FCSTD DOCUMENT  (FreeCAD 0.21R33668 +26 (Git))
Label: RotateEngine-000
License: All rights reserved
LicenseURL: http://en.wikipedia.org/wiki/All_rights_reserved
objects: App::DocumentObjectGroup×3, PartDesign::CoordinateSystem×2, Sketcher::SketchObject×2, App::FeaturePython×1, App::Part×1
note: 4 computed .brp shape members not serialized (recipe doc carries the construction recipe); baked Part::Feature solids carry a one-line shape summary decoded from their .brp

FEATURE [App::DocumentObjectGroup] Parts
FEATURE [PartDesign::CoordinateSystem] LCS_Origin
  AttacherType = Attacher::AttachEngine3D
  MapMode = 3
  Placement = pos=(0,0,0) rot=(1,0,0;3.14159rad)
  Support = -> [XZ_Plane]
FEATURE [App::DocumentObjectGroup] Constraints
FEATURE [App::FeaturePython] Variables  # WARN: FeaturePython — macro-defined, semantics opaque (R4)
  Angle_Rotation = 339
  Type = App::PropertyContainer
FEATURE [App::DocumentObjectGroup] Configurations
FEATURE [Sketcher::SketchObject] Barre  label="Sketch_Engine"
  AttachmentOffset = pos=(0,0,0) rot=(0,0,1;5.91667rad)
  FullyConstrained = false
  MapMode = 3
  Placement = pos=(0,0,0) rot=(0.967324,0.179283,0.179283;4.67917rad)
  Support = -> [LCS_Origin]
  expr: .AttachmentOffset.Rotation.Angle = Variables.Angle_Rotation
  sketch-geometry (2):
    g0: Circle CenterX=0 CenterY=0 CenterZ=0 NormalX=0 NormalY=0 NormalZ=1 AngleXU=0 Radius=20
    g1: LineSegment StartX=0 StartY=0 StartZ=0 EndX=17.8904 EndY=8.94064 EndZ=0
  constraints (4):
    c: Coincident(g0,g-1)
    c: Radius(g0) = 20
    c: Coincident(g1,g0)
    c: PointOnObject(g1,g0)
FEATURE [PartDesign::CoordinateSystem] LCS_Mobile
  AttacherType = Attacher::AttachEngine3D
  AttachmentOffset = pos=(40,0,0) rot=(0,0,1;0rad)
  MapMode = 3
  Placement = pos=(40,0,0) rot=(1,0,0;3.14159rad)
  Support = -> [XZ_Plane]
FEATURE [Sketcher::SketchObject] Sketch_Mobile
  ExternalGeometry = -> [Barre]
  FullyConstrained = true
  MapMode = 3
  Placement = pos=(40,0,0) rot=(-1,0,0;1.5708rad)
  Support = -> [LCS_Mobile]
  sketch-geometry (1):
    g0: LineSegment StartX=-20.0939 StartY=1.93547 StartZ=0 EndX=69.8853 EndY=0 EndZ=0
  constraints (3):
    c: Distance(g0) = 90
    c: PointOnObject(g0,g-1)
    c: Coincident(g0,g-3)
FEATURE [App::Part] Assembly
  AssemblyType = Part::Link
  Group = -> [LCS_Origin,Constraints,Variables,Configurations,Barre,LCS_Mobile,Sketch_Mobile]
  Origin = -> Origin
  Type = Assembly
